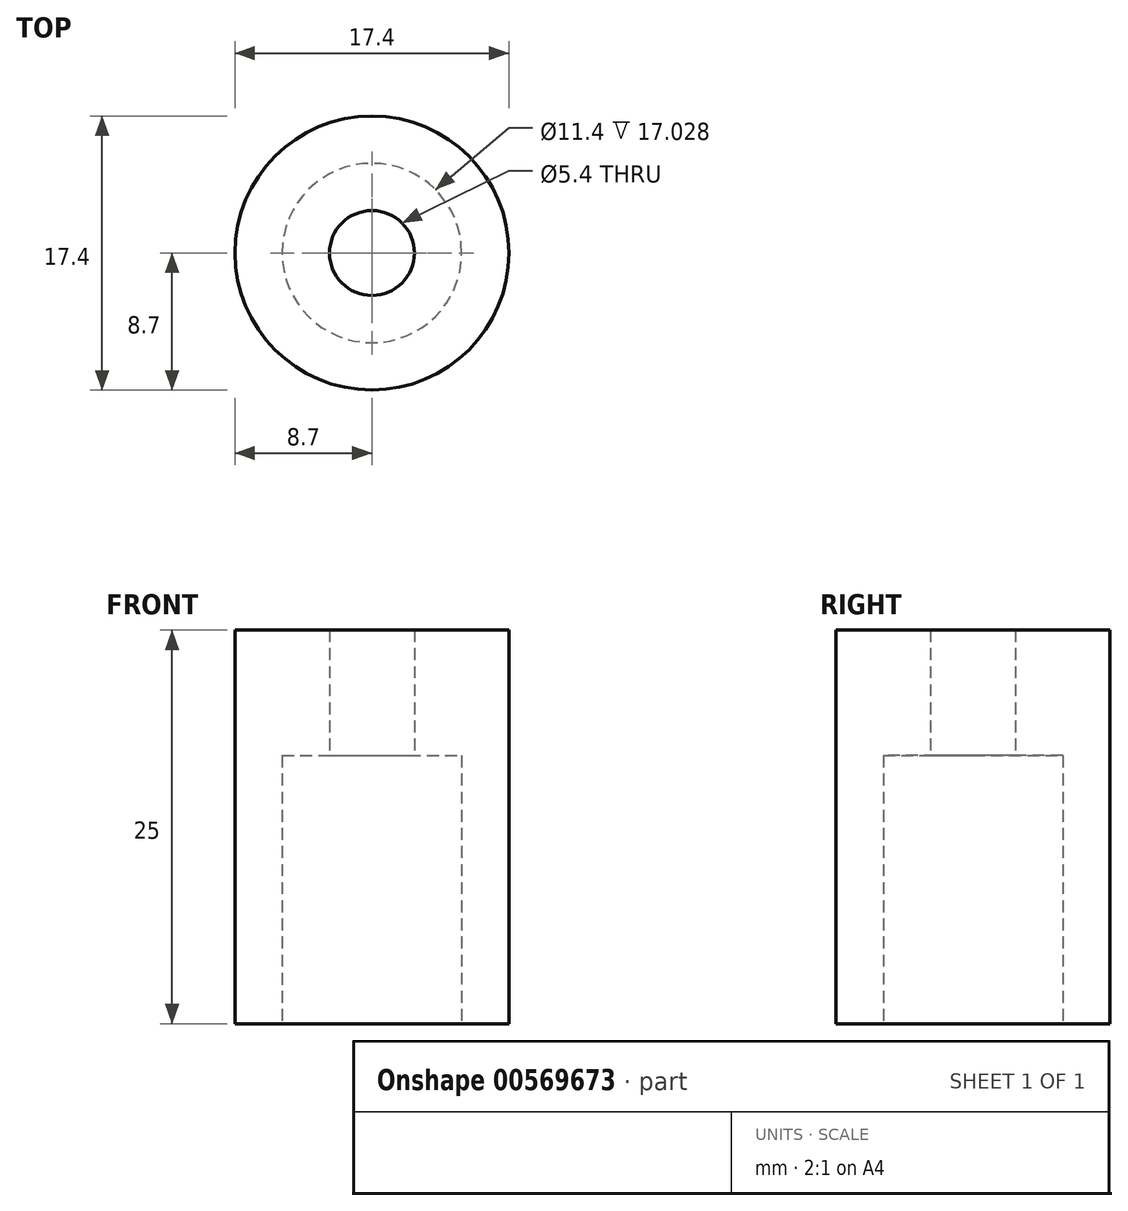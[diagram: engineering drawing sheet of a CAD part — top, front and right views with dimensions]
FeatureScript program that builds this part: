
annotation { "Feature Type Name" : "Feature", "Feature Type Description" : "" }
export const myFeature = defineFeature(function(context is Context, id is Id, definition is map)
    precondition{}
    {
        {
            var Q0;
            Q0=qCreatedBy(makeId("Front.planeOp"),FACE);
            var sketch = newSketch(context, id + "F0", { "sketchPlane" : qUnion([Q0])});
            skLineSegment(sketch, "E0", {"start": v(2.7, 24.97) * mm, "end": v(8.7, 24.97) * mm});
            skLineSegment(sketch, "E1", {"start": v(8.7, -0.03) * mm, "end": v(5.7, -0.03) * mm});
            skLineSegment(sketch, "E2", {"start": v(5.7, -0.03) * mm, "end": v(5.7, 17) * mm});
            skLineSegment(sketch, "E3", {"start": v(5.7, 17) * mm, "end": v(2.7, 17) * mm});
            skLineSegment(sketch, "E4", {"start": v(2.7, 17) * mm, "end": v(2.7, 24.97) * mm});
            skLineSegment(sketch, "E5", {"start": v(8.7, -0.03) * mm, "end": v(8.7, 24.97) * mm});
            skLineSegment(sketch, "E6", {"start": v(0, 21.58) * mm, "end": v(0, 31.54) * mm});
            skSolve(sketch);
        }
        {
            var Q0;
            Q0=makeQuery(id+"F0.imprint","IMPRINT",FACE,{"disambiguationData":[TD([[makeQuery(id+"F0.imprint","IMPRINT",EDGE,{"derivedFrom":sQuery(id+"F0.wireOp",EDGE,"E0")}),-1.0]])]});
            var Q1;
            Q1=sQuery(id+"F0.wireOp",EDGE,"E6");
            revolve(context, id + "F1", {"entities" : qUnion([Q0]), "axis" : qUnion([Q1]), "revolveType" : RevolveType.FULL});
        }
    });
